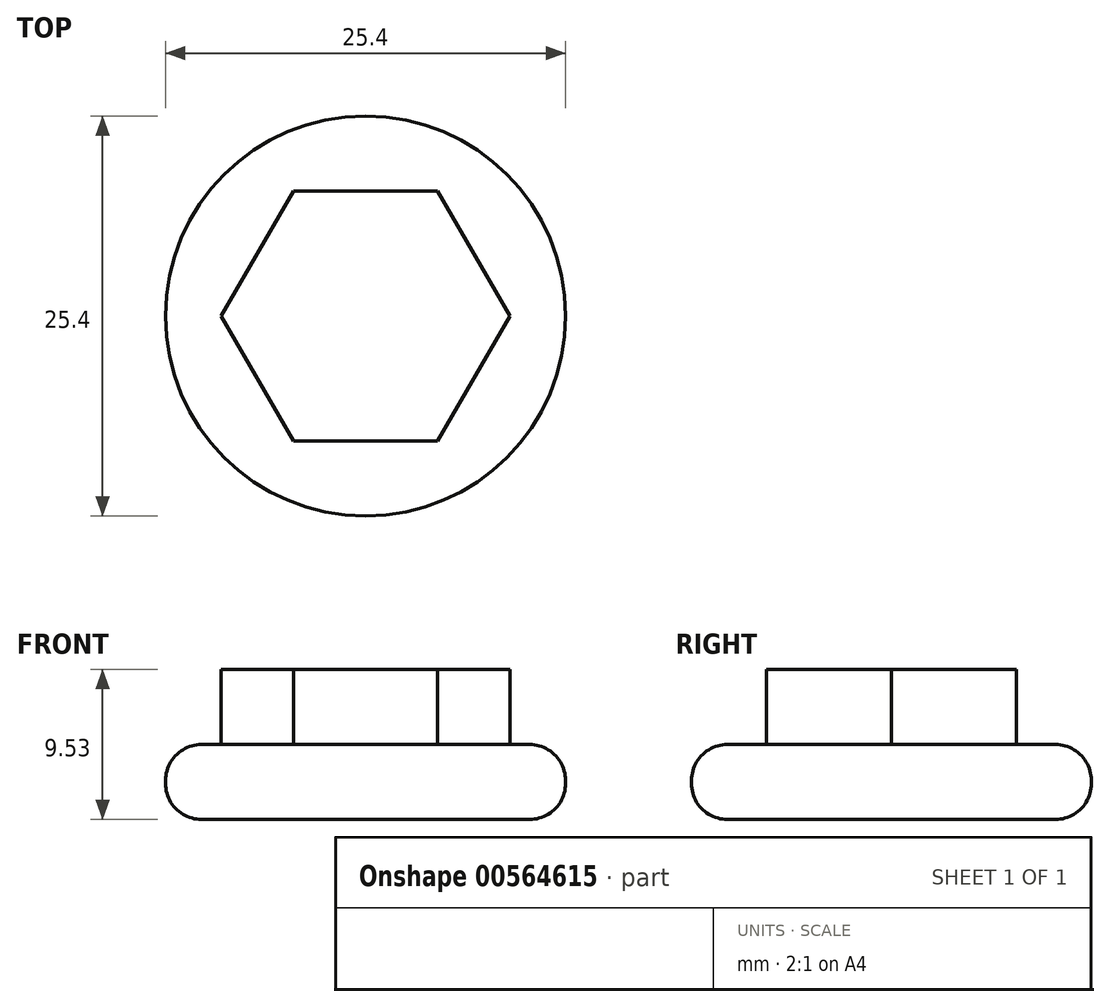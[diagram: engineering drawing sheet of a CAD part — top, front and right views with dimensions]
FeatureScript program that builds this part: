
annotation { "Feature Type Name" : "Feature", "Feature Type Description" : "" }
export const myFeature = defineFeature(function(context is Context, id is Id, definition is map)
    precondition{}
    {
        {
            var Q0;
            Q0=qCreatedBy(makeId("Top.planeOp"),FACE);
            var sketch = newSketch(context, id + "F0", { "sketchPlane" : qUnion([Q0])});
            skCircle(sketch, "E0", {"center": v(0, 0) * mm, "radius": 12.7 * mm});
            skSolve(sketch);
        }
        {
            var Q0;
            Q0=qSketchRegion(id+"F0",true);
            extrude(context, id + "F1", {"entities" : qUnion([Q0]), "flatOperationType" : FlatOperationType.REMOVE, "depth" : 4.76 * mm, "offsetDistance" : 25.4 * mm, "domain" : OperationDomain.MODEL});
        }
        {
            var Q0;
            Q0=makeQuery(id+"F1.opExtrude","CAP_FACE",FACE,{"disambiguationData":[OSD([sQuery(id+"F0.wireOp",EDGE,"E0")])],"isStart":false});
            var sketch = newSketch(context, id + "F2", { "sketchPlane" : qUnion([Q0])});
            skCircle(sketch, "E1.cCircle", {"center": v(0, 0) * mm, "radius": 7.94 * mm, "construction": true});
            skLineSegment(sketch, "E1.0", {"start": v(-4.58, 7.94) * mm, "end": v(4.58, 7.94) * mm});
            skLineSegment(sketch, "E1.1", {"start": v(4.58, 7.94) * mm, "end": v(9.17, 0) * mm});
            skLineSegment(sketch, "E1.2", {"start": v(9.17, 0) * mm, "end": v(4.58, -7.94) * mm});
            skLineSegment(sketch, "E1.3", {"start": v(4.58, -7.94) * mm, "end": v(-4.58, -7.94) * mm});
            skLineSegment(sketch, "E1.4", {"start": v(-4.58, -7.94) * mm, "end": v(-9.17, 0) * mm});
            skLineSegment(sketch, "E1.5", {"start": v(-9.17, 0) * mm, "end": v(-4.58, 7.94) * mm});
            skPoint(sketch, "E1.0.midPoint", {"position": v(0, 7.94) * mm});
            skSolve(sketch);
        }
        {
            var Q0;
            Q0=makeQuery(id+"F2.imprint","IMPRINT",FACE,{"disambiguationData":[TD([[makeQuery(id+"F2.imprint","IMPRINT",EDGE,{"derivedFrom":sQuery(id+"F2.wireOp",EDGE,"E1.0")}),-1.0]])]});
            extrude(context, id + "F3", {"entities" : qUnion([Q0]), "operationType" : NewBodyOperationType.ADD, "flatOperationType" : FlatOperationType.REMOVE, "depth" : 4.76 * mm, "offsetDistance" : 25.4 * mm, "domain" : OperationDomain.MODEL});
        }
        {
            var Q0;
            Q0=makeQuery(id+"F1.opExtrude","CAP_EDGE",EDGE,{"disambiguationData":[OSD([sQuery(id+"F0.wireOp",EDGE,"E0")])],"isStart":false});
            fillet(context, id + "F4", {"entities" : qUnion([Q0]), "radius" : 2.3 * mm, "tangentPropagation" : true, "allowEdgeOverflow" : false});
        }
        {
            var Q0;
            Q0=makeQuery(id+"F1.opExtrude","CAP_EDGE",EDGE,{"disambiguationData":[OSD([sQuery(id+"F0.wireOp",EDGE,"E0")])],"isStart":true});
            fillet(context, id + "F5", {"entities" : qUnion([Q0]), "radius" : 2.3 * mm, "tangentPropagation" : true, "allowEdgeOverflow" : false});
        }
    });
